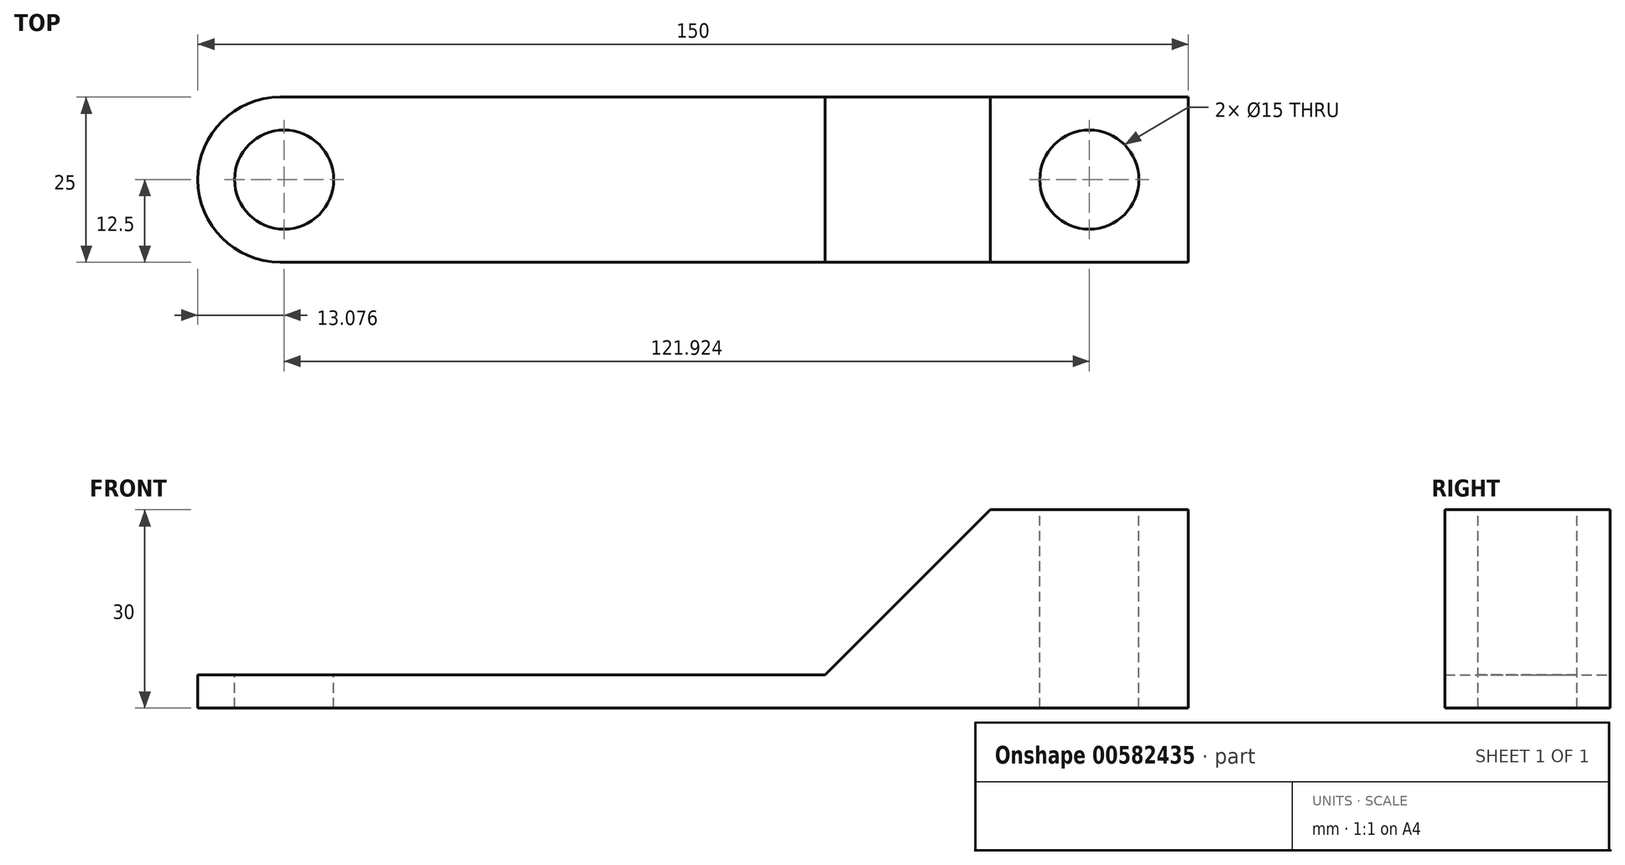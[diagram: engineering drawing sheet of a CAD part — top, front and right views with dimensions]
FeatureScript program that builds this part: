
annotation { "Feature Type Name" : "Feature", "Feature Type Description" : "" }
export const myFeature = defineFeature(function(context is Context, id is Id, definition is map)
    precondition{}
    {
        {
            var Q0;
            Q0=qCreatedBy(makeId("Front.planeOp"),FACE);
            var sketch = newSketch(context, id + "F0", { "sketchPlane" : qUnion([Q0])});
            skLineSegment(sketch, "E0", {"start": v(0, 0) * mm, "end": v(0, 30) * mm});
            skLineSegment(sketch, "E1", {"start": v(0, 30) * mm, "end": v(-30, 30) * mm});
            skLineSegment(sketch, "E2", {"start": v(-30, 30) * mm, "end": v(-55, 5) * mm});
            skLineSegment(sketch, "E3", {"start": v(-55, 5) * mm, "end": v(-150, 5) * mm});
            skLineSegment(sketch, "E4", {"start": v(-150, 5) * mm, "end": v(-150, 0) * mm});
            skLineSegment(sketch, "E5", {"start": v(-150, 0) * mm, "end": v(0, 0) * mm});
            skSolve(sketch);
        }
        {
            var Q0;
            Q0 = qSketchRegion(id + "F0", true);
            extrude(context, id + "F1", {"entities" : qUnion([Q0]), "endBound" : BoundingType.SYMMETRIC, "depth" : 25 * mm, "offsetDistance" : 25 * mm});
        }
        {
            var Q0;
            Q0=makeQuery(id+"F1.opExtrude","SWEPT_FACE",FACE,{"disambiguationData":[OSD([sQuery(id+"F0.wireOp",EDGE,"E1")])]});
            var sketch = newSketch(context, id + "F2", { "sketchPlane" : qUnion([Q0])});
            skCircle(sketch, "E6", {"center": v(-15, 0) * mm, "radius": 7.5 * mm});
            skPoint(sketch, "E6.centerSnap0", {"position": v(-15, 12.5) * mm});
            skSolve(sketch);
        }
        {
            var Q0;
            Q0 = qSketchRegion(id + "F2", true);
            var Q1;
            Q1=makeQuery(id+"F1.opExtrude","SWEPT_FACE",FACE,{"disambiguationData":[OSD([sQuery(id+"F0.wireOp",EDGE,"E5")])]});
            extrude(context, id + "F3", {"entities" : qUnion([Q0]), "operationType" : NewBodyOperationType.REMOVE, "endBound" : BoundingType.UP_TO_SURFACE, "oppositeDirection" : true, "depth" : 25 * mm, "endBoundEntityFace" : qUnion([Q1]), "offsetDistance" : 25 * mm});
        }
        {
            var Q0;
            Q0=makeQuery(id+"F1.opExtrude","SWEPT_FACE",FACE,{"disambiguationData":[OSD([sQuery(id+"F0.wireOp",EDGE,"E3")])]});
            var sketch = newSketch(context, id + "F4", { "sketchPlane" : qUnion([Q0])});
            skCircle(sketch, "E7", {"center": v(-136.92, 0) * mm, "radius": 7.5 * mm});
            skSolve(sketch);
        }
        {
            var Q0;
            Q0=makeQuery(id+"F1.opExtrude","CAP_EDGE",EDGE,{"disambiguationData":[OSD([sQuery(id+"F0.wireOp",EDGE,"E4")])],"isStart":true});
            var Q1;
            Q1=makeQuery(id+"F1.opExtrude","CAP_EDGE",EDGE,{"disambiguationData":[OSD([sQuery(id+"F0.wireOp",EDGE,"E4")])],"isStart":false});
            fillet(context, id + "F5", {"entities" : qUnion([Q0, Q1]), "radius" : (25 / 2) * mm, "tangentPropagation" : true, "allowEdgeOverflow" : false});
        }
        {
            var Q0;
            Q0=makeQuery(id+"F4.imprint","IMPRINT",FACE,{"disambiguationData":[TD([[makeQuery(id+"F4.imprint","IMPRINT",EDGE,{"derivedFrom":sQuery(id+"F4.wireOp",EDGE,"E7")}),1.0]])]});
            extrude(context, id + "F6", {"entities" : qUnion([Q0]), "operationType" : NewBodyOperationType.REMOVE, "endBound" : BoundingType.UP_TO_NEXT, "oppositeDirection" : true, "depth" : 25 * mm, "offsetDistance" : 25 * mm});
        }
    });
